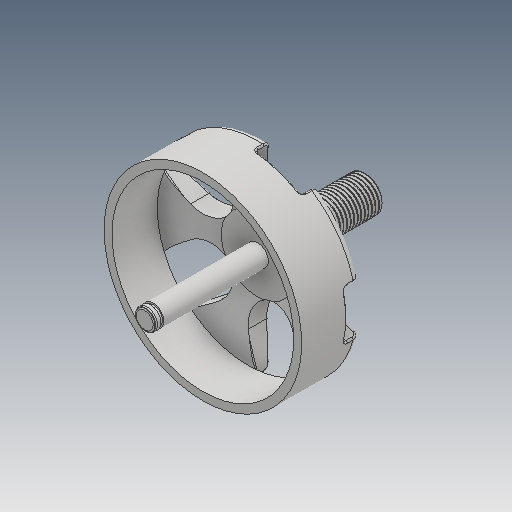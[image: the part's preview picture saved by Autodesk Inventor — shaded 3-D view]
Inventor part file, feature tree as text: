
AUTODESK INVENTOR PART (.ipt)
format: ipt  version: 2018 (Build 220112000, 112)  size: 892,928 bytes
history: native  units: mm
features: fillet x1
ambient origin geometry x8: Origin, YZ Plane, XZ Plane, XY Plane, X Axis, Y Axis, Z Axis, Center Point
bodies: Volumenkörper1 (feature_tree)
feature tree (1):
  fillet  "Fillet7"  [1 undecoded]
note: 1 required parameter value undecoded (feature->parameter linkage not recoverable at this tier; creation-order binding heuristic only, values carry confidence <= 0.55)
